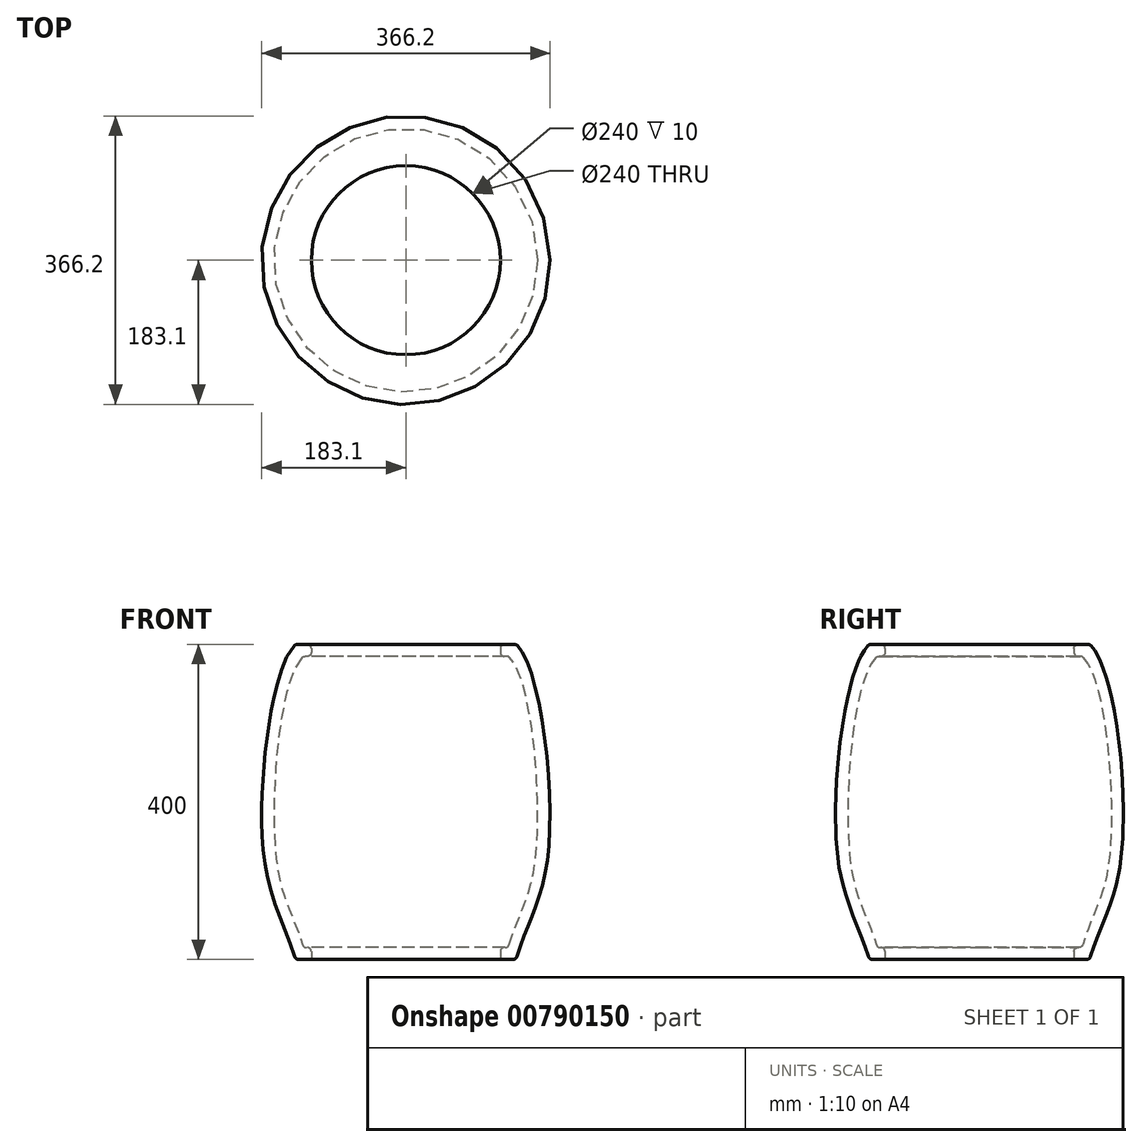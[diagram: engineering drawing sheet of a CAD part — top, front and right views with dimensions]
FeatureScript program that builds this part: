
annotation { "Feature Type Name" : "Feature", "Feature Type Description" : "" }
export const myFeature = defineFeature(function(context is Context, id is Id, definition is map)
    precondition{}
    {
        {
            var Q0;
            Q0=qCreatedBy(makeId("Right.planeOp"),FACE);
            var sketch = newSketch(context, id + "F0", { "sketchPlane" : qUnion([Q0])});
            skLineSegment(sketch, "E0", {"start": v(0, 0) * mm, "end": v(-140, 0) * mm});
            skFitSpline(sketch, "E1", {"points": [v(-140, 0) * mm, v(-181.38, 140.4) * mm, v(-140, 400) * mm], "startDerivative": vector(-100.87, 334.97) * mm, "endDerivative": vector(154.55, 126.72) * mm});
            skLineSegment(sketch, "E2", {"start": v(0, 0) * mm, "end": v(0, 400) * mm});
            skLineSegment(sketch, "E3", {"start": v(0, 15) * mm, "end": v(-130, 15) * mm});
            skFitSpline(sketch, "E4", {"points": [v(-130, 15) * mm, v(-164.88, 129.1) * mm, v(-130, 385) * mm], "startDerivative": vector(-100.87, 334.97) * mm, "endDerivative": vector(154.55, 126.72) * mm});
            skLineSegment(sketch, "E5", {"start": v(0, 185) * mm, "end": v(0, 15) * mm});
            skLineSegment(sketch, "E6", {"start": v(0, 400) * mm, "end": v(-140, 400) * mm});
            skLineSegment(sketch, "E7", {"start": v(0, 385) * mm, "end": v(-130, 385) * mm});
            skSolve(sketch);
        }
        {
            var Q0;
            {var subQ3=sQuery(id+"F0.wireOp",EDGE,"E0");Q0=makeQuery(id+"F0.imprint","IMPRINT",FACE,{"disambiguationData":[TD([[makeQuery(id+"F0.imprint","IMPRINT",EDGE,{"derivedFrom":subQ3}),-1.0]])]});}
            var Q1;
            Q1=sQuery(id+"F0.wireOp",EDGE,"E5");
            revolve(context, id + "F1", {"surfaceOperationType" : NewSurfaceOperationType.NEW, "entities" : qUnion([Q0]), "axis" : qUnion([Q1]), "revolveType" : RevolveType.FULL});
        }
        {
            var Q0;
            Q0=makeQuery(id+"F1.opRevolve","SWEPT_FACE",FACE,{"disambiguationData":[OSD([sQuery(id+"F0.wireOp",EDGE,"E0")])]});
            var sketch = newSketch(context, id + "F2", { "sketchPlane" : qUnion([Q0])});
            skCircle(sketch, "E8", {"center": v(0, 0) * mm, "radius": 120 * mm});
            skSolve(sketch);
        }
        {
            var Q0;
            Q0 = qSketchRegion(id + "F2", true);
            extrude(context, id + "F3", {"entities" : qUnion([Q0]), "operationType" : NewBodyOperationType.REMOVE, "endBound" : BoundingType.THROUGH_ALL, "oppositeDirection" : true, "depth" : 25 * mm, "offsetDistance" : 25 * mm});
        }
        {
            var Q0;
            {var subQ0=makeQuery(id+"F3.opExtrude","SWEPT_FACE",FACE,{"disambiguationData":[OSD([sQuery(id+"F2.wireOp",EDGE,"E8")])]});Q0=qUnion([makeQuery(id+"F3.boolean.opBoolean","INTERSECT",EDGE,{"derivedFrom":[makeQuery(id+"F1.opRevolve","SWEPT_FACE",FACE,{"disambiguationData":[OSD([sQuery(id+"F0.wireOp",EDGE,"E3")])]}),subQ0]}),makeQuery(id+"F3.boolean.opBoolean","INTERSECT",EDGE,{"derivedFrom":[makeQuery(id+"F1.opRevolve","SWEPT_FACE",FACE,{"disambiguationData":[OSD([sQuery(id+"F0.wireOp",EDGE,"E6")])]}),subQ0]}),makeQuery(id+"F3.boolean.opBoolean","INTERSECT",EDGE,{"derivedFrom":[makeQuery(id+"F1.opRevolve","SWEPT_FACE",FACE,{"disambiguationData":[OSD([sQuery(id+"F0.wireOp",EDGE,"E7")])]}),subQ0]})]);}
            var Q1;
            {var subQ0=sQuery(id+"F0.wireOp",EDGE,"E1");Q1=qUnion([makeQuery(id+"F1.opRevolve","SWEPT_EDGE",EDGE,{"disambiguationData":[OSD([sQuery(id+"F0.wireOp",EDGE,"E0"),subQ0])]}),makeQuery(id+"F1.opRevolve","SWEPT_EDGE",EDGE,{"disambiguationData":[OSD([subQ0,sQuery(id+"F0.wireOp",EDGE,"E6")])]})]);}
            var Q2;
            Q2=makeQuery(id+"F1.opRevolve","SWEPT_EDGE",EDGE,{"disambiguationData":[OSD([sQuery(id+"F0.wireOp",EDGE,"E0"),sQuery(id+"F0.wireOp",EDGE,"E1")])]});
            var Q3;
            Q3=makeQuery(id+"F3.boolean.opBoolean","COPY",EDGE,{"derivedFrom":makeQuery(id+"F3.opExtrude","CAP_EDGE",EDGE,{"disambiguationData":[OSD([sQuery(id+"F2.wireOp",EDGE,"E8")])],"isStart":true})});
            fillet(context, id + "F4", {"entities" : qUnion([Q0, Q1, Q2, Q3]), "radius" : 5 * mm, "tangentPropagation" : true, "allowEdgeOverflow" : false});
        }
        {
            var Q0;
            {var subQ0=sQuery(id+"F0.wireOp",EDGE,"E4");Q0=qUnion([makeQuery(id+"F1.opRevolve","SWEPT_EDGE",EDGE,{"disambiguationData":[OSD([sQuery(id+"F0.wireOp",EDGE,"E3"),subQ0])]}),makeQuery(id+"F1.opRevolve","SWEPT_EDGE",EDGE,{"disambiguationData":[OSD([subQ0,sQuery(id+"F0.wireOp",EDGE,"E7")])]})]);}
            var Q1;
            Q1=makeQuery(id+"F1.opRevolve","SWEPT_EDGE",EDGE,{"disambiguationData":[OSD([sQuery(id+"F0.wireOp",EDGE,"E3"),sQuery(id+"F0.wireOp",EDGE,"E4")])]});
            fillet(context, id + "F5", {"entities" : qUnion([Q0, Q1]), "radius" : 5 * mm, "tangentPropagation" : true, "allowEdgeOverflow" : false});
        }
    });
